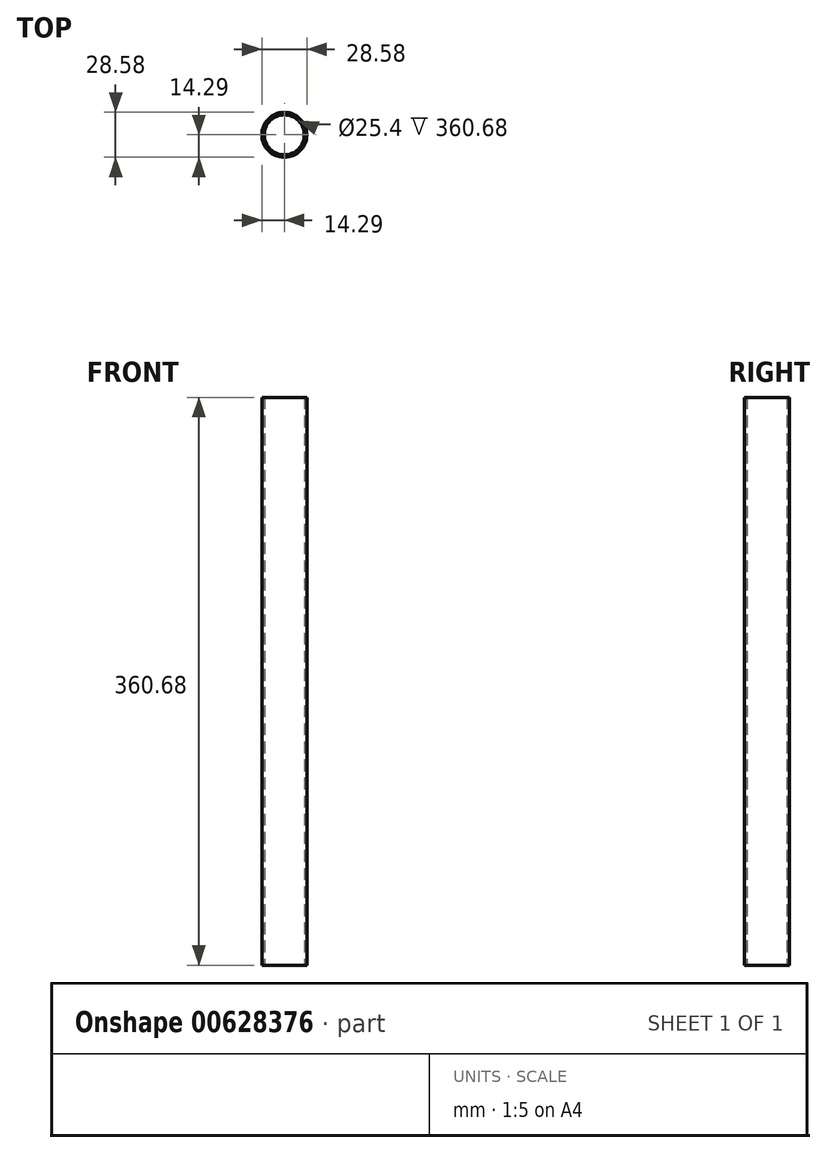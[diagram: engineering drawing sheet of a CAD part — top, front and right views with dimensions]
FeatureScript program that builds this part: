
annotation { "Feature Type Name" : "Feature", "Feature Type Description" : "" }
export const myFeature = defineFeature(function(context is Context, id is Id, definition is map)
    precondition{}
    {
        {
            var Q0;
            Q0=qCreatedBy(makeId("Top.planeOp"),FACE);
            var sketch = newSketch(context, id + "F0", { "sketchPlane" : qUnion([Q0])});
            skLineSegment(sketch, "E0", {"start": v(0, 0) * mm, "end": v(12.7, 0) * mm});
            skCircle(sketch, "E1", {"center": v(0, 0) * mm, "radius": 12.7 * mm});
            skCircle(sketch, "E2.0", {"center": v(0, 0) * mm, "radius": 14.29 * mm});
            skSolve(sketch);
        }
        {
            var Q0;
            Q0=qCreatedBy(makeId("Top.planeOp"),FACE);
            var sketch = newSketch(context, id + "F1", { "sketchPlane" : qUnion([Q0])});
            skSolve(sketch);
        }
        {
            var Q0;
            Q0=qSketchRegion(id+"F1",true);
            var Q1;
            Q1=makeQuery(id+"F0.imprint","IMPRINT",FACE,{"disambiguationData":[TD([[makeQuery(id+"F0.imprint","IMPRINT",EDGE,{"derivedFrom":sQuery(id+"F0.wireOp",EDGE,"E1")}),-1.0]])]});
            extrude(context, id + "F2", {"entities" : qUnion([Q0, Q1]), "depth" : 360.68 * mm, "offsetDistance" : 25.4 * mm});
        }
    });
